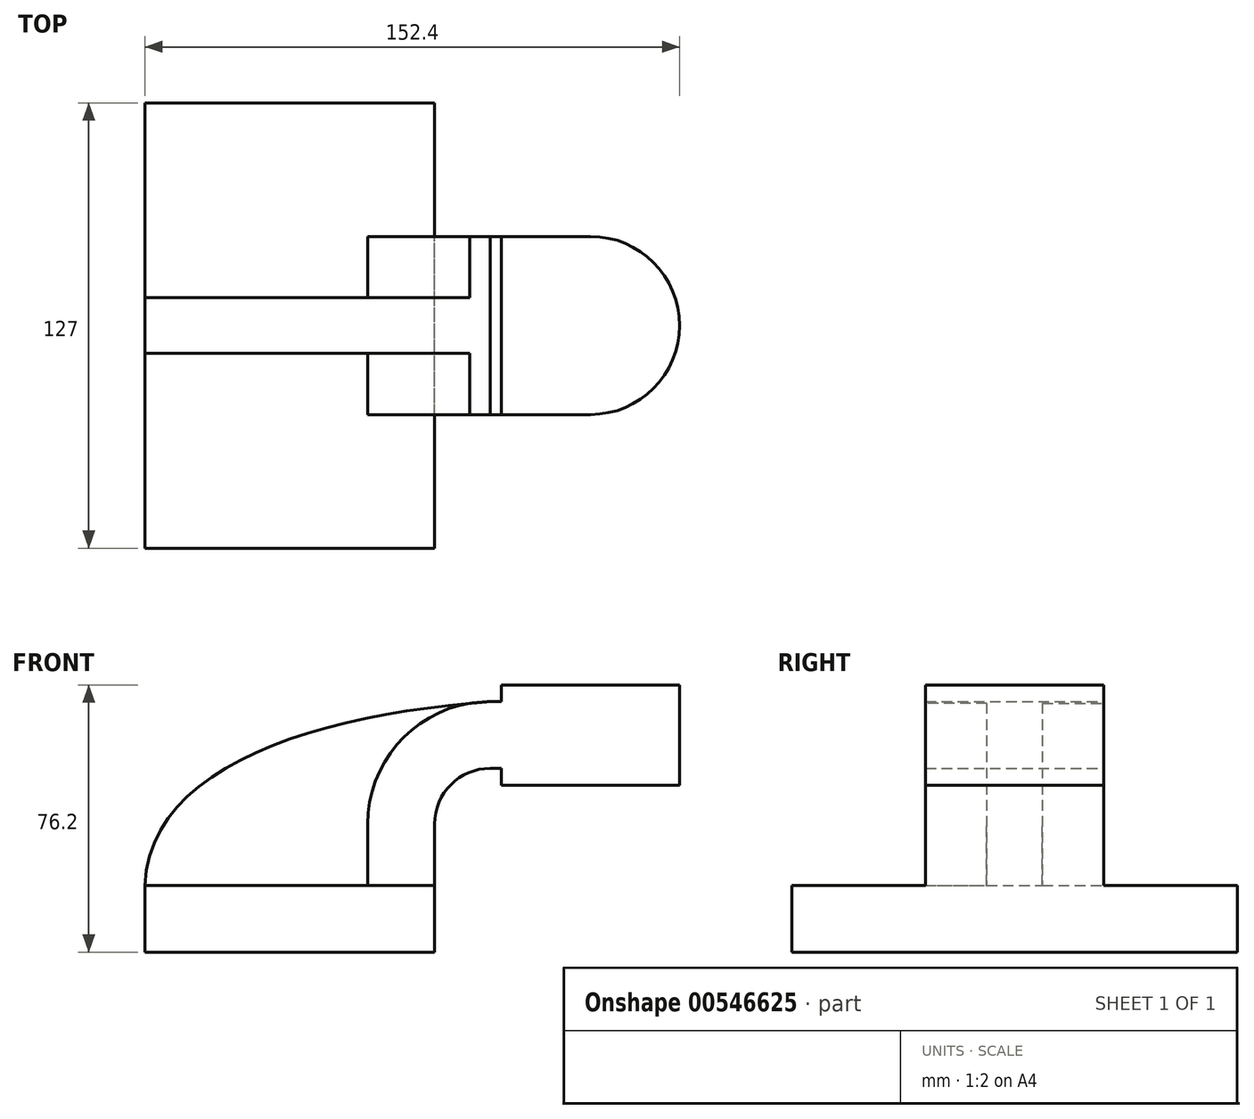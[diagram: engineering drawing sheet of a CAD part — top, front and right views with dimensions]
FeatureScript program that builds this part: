
annotation { "Feature Type Name" : "Feature", "Feature Type Description" : "" }
export const myFeature = defineFeature(function(context is Context, id is Id, definition is map)
    precondition{}
    {
        {
            var Q0;
            Q0=qCreatedBy(makeId("Front.planeOp"),FACE);
            var sketch = newSketch(context, id + "F0", { "sketchPlane" : qUnion([Q0])});
            skLineSegment(sketch, "E0.bottom", {"start": v(41.27, 9.53) * mm, "end": v(-41.27, 9.53) * mm});
            skLineSegment(sketch, "E0.top", {"start": v(41.28, -9.52) * mm, "end": v(-41.27, -9.52) * mm});
            skLineSegment(sketch, "E0.left", {"start": v(41.28, 9.53) * mm, "end": v(41.28, -9.52) * mm});
            skLineSegment(sketch, "E0.right", {"start": v(-41.27, 9.53) * mm, "end": v(-41.27, -9.52) * mm});
            skPoint(sketch, "E0.middle", {"position": v(0, 0) * mm});
            skLineSegment(sketch, "E1.bottom", {"start": v(111.12, 66.68) * mm, "end": v(60.32, 66.68) * mm});
            skLineSegment(sketch, "E1.top", {"start": v(111.12, 38.1) * mm, "end": v(60.33, 38.1) * mm});
            skLineSegment(sketch, "E1.left", {"start": v(111.12, 66.68) * mm, "end": v(111.12, 38.1) * mm});
            skLineSegment(sketch, "E1.right", {"start": v(60.32, 66.68) * mm, "end": v(60.32, 38.1) * mm});
            skPoint(sketch, "E1.middle", {"position": v(85.72, 52.39) * mm});
            skLineSegment(sketch, "E2", {"start": v(41.27, 9.53) * mm, "end": v(41.27, 27) * mm});
            skArc(sketch, "E3", {"start": v(41.27, 27) * mm, "mid": v(45.92, 38.23) * mm, "end": v(57.15, 42.88) * mm});
            skLineSegment(sketch, "E4", {"start": v(57.15, 42.88) * mm, "end": v(85.72, 42.88) * mm});
            skLineSegment(sketch, "E5.0", {"start": v(57.15, 61.93) * mm, "end": v(85.72, 61.93) * mm});
            skArc(sketch, "E5.1", {"start": v(22.22, 27) * mm, "mid": v(32.45, 51.7) * mm, "end": v(57.15, 61.93) * mm});
            skLineSegment(sketch, "E5.2", {"start": v(22.22, 9.53) * mm, "end": v(22.22, 27) * mm});
            skLineSegment(sketch, "E6", {"start": v(85.72, 38.1) * mm, "end": v(85.72, 66.68) * mm});
            skFitSpline(sketch, "E7", {"points": [v(57.15, 61.93) * mm, v(-41.28, 9.52) * mm], "startDerivative": vector(-145.91, -10.96) * mm, "endDerivative": vector(-4.21, -103.67) * mm});
            skSolve(sketch);
        }
        {
            var Q0;
            Q0=makeQuery(id+"F0.imprint","IMPRINT",FACE,{"disambiguationData":[TD([[makeQuery(id+"F0.imprint","IMPRINT",EDGE,{"derivedFrom":sQuery(id+"F0.wireOp",EDGE,"E0.top")}),-1.0]])]});
            extrude(context, id + "F1", {"entities" : qUnion([Q0]), "endBound" : BoundingType.SYMMETRIC, "depth" : 127 * mm, "offsetDistance" : 25.4 * mm});
        }
        {
            var Q0;
            {var subQ1=sQuery(id+"F0.wireOp",EDGE,"E2");Q0=makeQuery(id+"F0.imprint","IMPRINT",FACE,{"disambiguationData":[TD([[makeQuery(id+"F0.imprint","IMPRINT",EDGE,{"derivedFrom":subQ1}),1.0]])]});}
            var Q1;
            {var subQ6=sQuery(id+"F0.wireOp",EDGE,"E6");Q1=makeQuery(id+"F0.imprint","IMPRINT",FACE,{"disambiguationData":[TD([[makeQuery(id+"F0.imprint","IMPRINT",EDGE,{"derivedFrom":subQ6}),1.0]])]});}
            var Q2;
            {var subQ5=sQuery(id+"F0.wireOp",EDGE,"E5.0");var subQ7=sQuery(id+"F0.wireOp",EDGE,"E1.right");var subQ8=makeQuery(id+"F0.imprint","INTERSECT",VERTEX,{"derivedFrom":[subQ7,subQ5]});Q2=makeQuery(id+"F0.imprint","IMPRINT",FACE,{"disambiguationData":[TD([[makeQuery(id+"F0.imprint","IMPRINT",EDGE,{"disambiguationData":[TD([[subQ8,-1.0]])],"derivedFrom":subQ7}),1.0]])]});}
            extrude(context, id + "F2", {"entities" : qUnion([Q0, Q1, Q2]), "operationType" : NewBodyOperationType.ADD, "endBound" : BoundingType.SYMMETRIC, "depth" : 50.8 * mm, "offsetDistance" : 25.4 * mm});
        }
        {
            var Q0;
            {var subQ3=sQuery(id+"F0.wireOp",EDGE,"E5.2");Q0=makeQuery(id+"F0.imprint","IMPRINT",FACE,{"disambiguationData":[TD([[makeQuery(id+"F0.imprint","IMPRINT",EDGE,{"derivedFrom":subQ3}),1.0]])]});}
            extrude(context, id + "F3", {"entities" : qUnion([Q0]), "operationType" : NewBodyOperationType.ADD, "endBound" : BoundingType.SYMMETRIC, "depth" : 15.88 * mm, "offsetDistance" : 25.4 * mm});
        }
        {
            var Q0;
            {var subQ4=sQuery(id+"F0.wireOp",EDGE,"E1.left");Q0=makeQuery(id+"F0.imprint","IMPRINT",FACE,{"disambiguationData":[TD([[makeQuery(id+"F0.imprint","IMPRINT",EDGE,{"derivedFrom":subQ4}),-1.0]])]});}
            var Q1;
            Q1=sQuery(id+"F0.wireOp",EDGE,"E6");
            revolve(context, id + "F4", {"operationType" : NewBodyOperationType.ADD, "entities" : qUnion([Q0]), "axis" : qUnion([Q1]), "revolveType" : RevolveType.SYMMETRIC, "oppositeDirection" : true, "angle" : 360 * degree});
        }
    });
